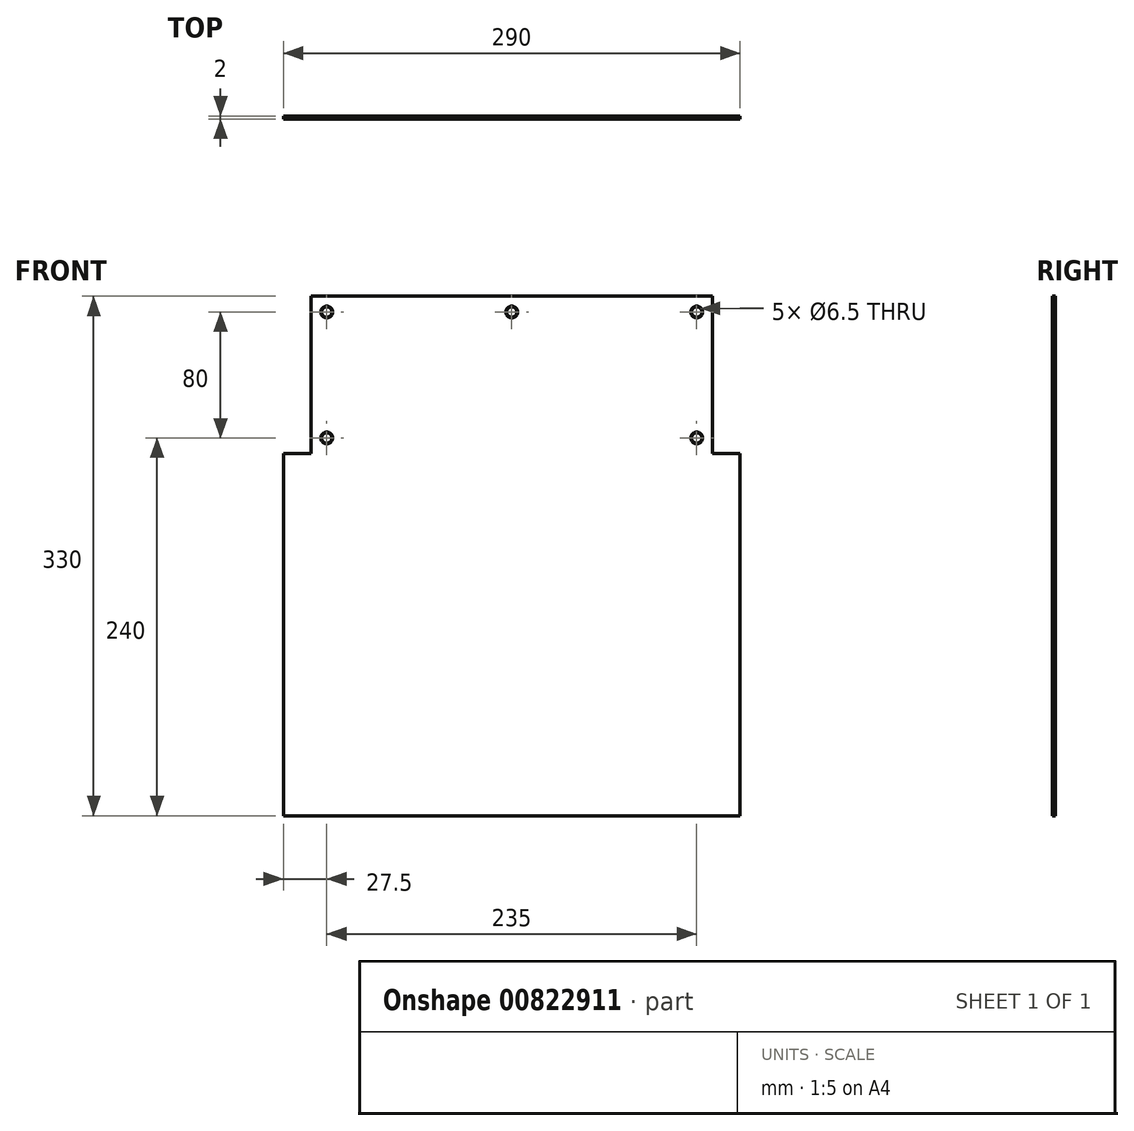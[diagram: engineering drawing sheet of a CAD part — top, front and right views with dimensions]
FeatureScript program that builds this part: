
annotation { "Feature Type Name" : "Feature", "Feature Type Description" : "" }
export const myFeature = defineFeature(function(context is Context, id is Id, definition is map)
    precondition{}
    {
        {
            var Q0;
            Q0=qCreatedBy(makeId("Front.planeOp"),FACE);
            var sketch = newSketch(context, id + "F0", { "sketchPlane" : qUnion([Q0])});
            skLineSegment(sketch, "E0.bottom", {"start": v(145, 115) * mm, "end": v(127.5, 115) * mm});
            skLineSegment(sketch, "E0.top", {"start": v(145, -115) * mm, "end": v(-145, -115) * mm});
            skLineSegment(sketch, "E0.left", {"start": v(145, 115) * mm, "end": v(145, -115) * mm});
            skLineSegment(sketch, "E0.right", {"start": v(-145, 115) * mm, "end": v(-145, -115) * mm});
            skPoint(sketch, "E0.middle", {"position": v(0, 0) * mm});
            skLineSegment(sketch, "E1", {"start": v(0, 0) * mm, "end": v(0, 165) * mm, "construction": true});
            skLineSegment(sketch, "E2.top", {"start": v(127.5, 215) * mm, "end": v(-127.5, 215) * mm});
            skLineSegment(sketch, "E2.left", {"start": v(127.5, 115) * mm, "end": v(127.5, 215) * mm});
            skLineSegment(sketch, "E2.right", {"start": v(-127.5, 115) * mm, "end": v(-127.5, 215) * mm});
            skPoint(sketch, "E2.middle", {"position": v(0, 165) * mm});
            skLineSegment(sketch, "E3.trimOffspring", {"start": v(-127.5, 115) * mm, "end": v(-145, 115) * mm});
            skLineSegment(sketch, "E4.bottom", {"start": v(-117.5, 205) * mm, "end": v(117.5, 205) * mm, "construction": true});
            skLineSegment(sketch, "E4.top", {"start": v(-117.5, 125) * mm, "end": v(117.5, 125) * mm, "construction": true});
            skLineSegment(sketch, "E4.left", {"start": v(-117.5, 205) * mm, "end": v(-117.5, 125) * mm, "construction": true});
            skLineSegment(sketch, "E4.right", {"start": v(117.5, 205) * mm, "end": v(117.5, 125) * mm, "construction": true});
            skCircle(sketch, "E5", {"center": v(-117.5, 205) * mm, "radius": 3.25 * mm});
            skCircle(sketch, "E6", {"center": v(-117.5, 125) * mm, "radius": 3.25 * mm});
            skCircle(sketch, "E7.MirrorC", {"center": v(117.5, 205) * mm, "radius": 3.25 * mm});
            skCircle(sketch, "E8.MirrorC", {"center": v(117.5, 125) * mm, "radius": 3.25 * mm});
            skCircle(sketch, "E9", {"center": v(0, 205) * mm, "radius": 3.25 * mm});
            skSolve(sketch);
        }
        {
            var Q0;
            Q0 = qSketchRegion(id + "F0", true);
            extrude(context, id + "F1", {"entities" : qUnion([Q0]), "depth" : 2 * mm, "offsetDistance" : 25 * mm});
        }
        {
            var Q0;
            Q0=makeQuery(id+"F1.opExtrude","SWEPT_FACE",FACE,{"disambiguationData":[OSD([sQuery(id+"F0.wireOp",EDGE,"E6")])]});
            var Q1;
            Q1=makeQuery(id+"F1.opExtrude","SWEPT_FACE",FACE,{"disambiguationData":[OSD([sQuery(id+"F0.wireOp",EDGE,"E5")])]});
            var Q2;
            Q2=makeQuery(id+"F1.opExtrude","SWEPT_FACE",FACE,{"disambiguationData":[OSD([sQuery(id+"F0.wireOp",EDGE,"E7.MirrorC")])]});
            var Q3;
            Q3=makeQuery(id+"F1.opExtrude","SWEPT_FACE",FACE,{"disambiguationData":[OSD([sQuery(id+"F0.wireOp",EDGE,"E8.MirrorC")])]});
            var Q4;
            Q4=makeQuery(id+"F1.opExtrude","SWEPT_FACE",FACE,{"disambiguationData":[OSD([sQuery(id+"F0.wireOp",EDGE,"E9")])]});
            chamfer(context, id + "F2", {"entities" : qUnion([Q0, Q1, Q2, Q3, Q4]), "width" : 0.5 * mm, "tangentPropagation" : true});
        }
    });
